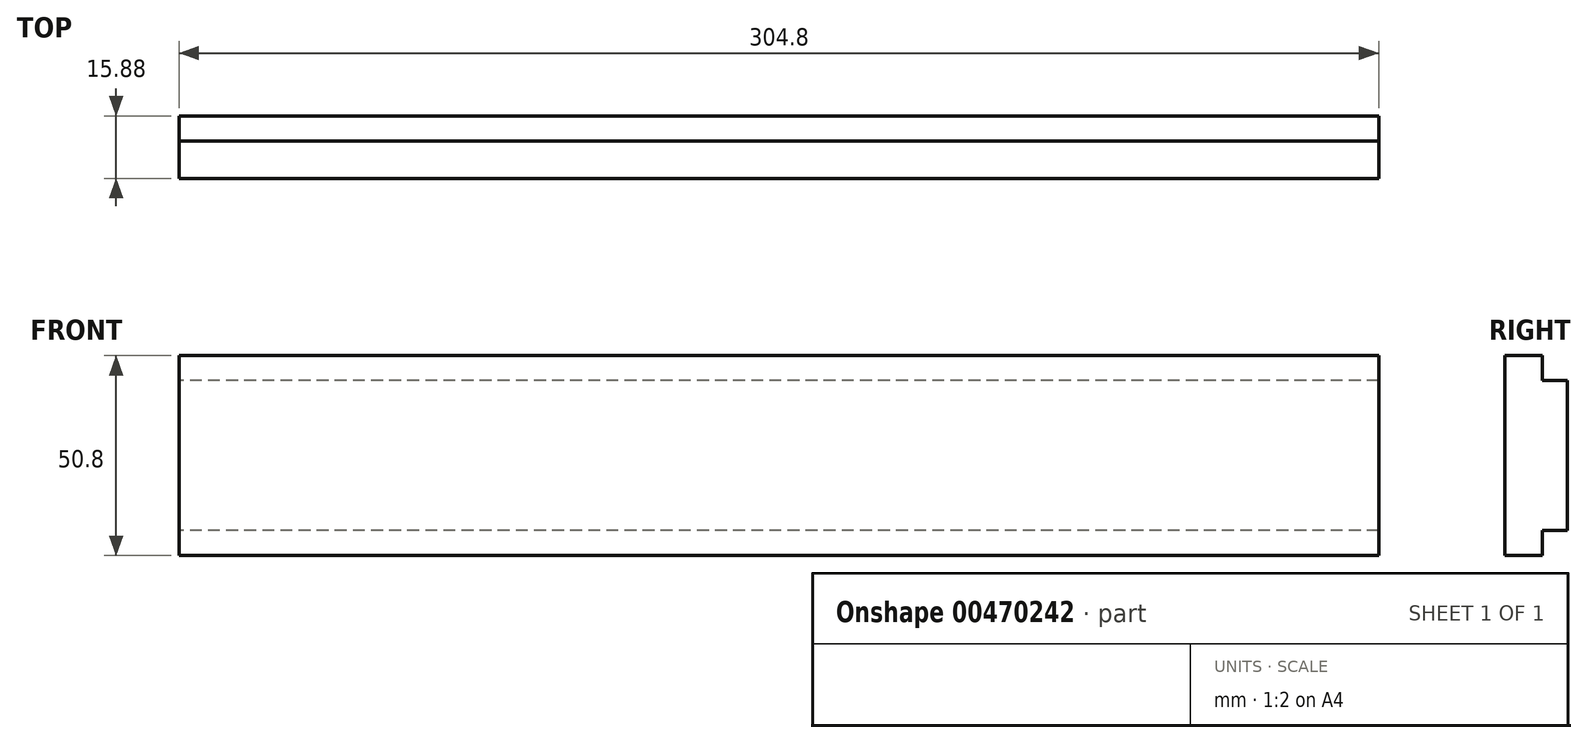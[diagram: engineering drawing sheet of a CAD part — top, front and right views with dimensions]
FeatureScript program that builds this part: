
annotation { "Feature Type Name" : "Feature", "Feature Type Description" : "" }
export const myFeature = defineFeature(function(context is Context, id is Id, definition is map)
    precondition{}
    {
        {
            var Q0;
            Q0=qCreatedBy(makeId("Right.planeOp"),FACE);
            var sketch = newSketch(context, id + "F0", { "sketchPlane" : qUnion([Q0])});
            skLineSegment(sketch, "E0.bottom", {"start": v(-20.64, 25.4) * mm, "end": v(-11.11, 25.4) * mm});
            skLineSegment(sketch, "E0.top", {"start": v(-20.64, -25.4) * mm, "end": v(-11.11, -25.4) * mm});
            skLineSegment(sketch, "E0.left", {"start": v(-20.64, 25.4) * mm, "end": v(-20.64, -25.4) * mm});
            skLineSegment(sketch, "E0.right", {"start": v(-11.11, 25.4) * mm, "end": v(-11.11, -25.4) * mm});
            skLineSegment(sketch, "E1.bottom", {"start": v(-11.11, -19.05) * mm, "end": v(-4.76, -19.05) * mm});
            skLineSegment(sketch, "E1.top", {"start": v(-11.11, 19.05) * mm, "end": v(-4.76, 19.05) * mm});
            skLineSegment(sketch, "E1.left", {"start": v(-11.11, -19.05) * mm, "end": v(-11.11, 19.05) * mm});
            skLineSegment(sketch, "E1.right", {"start": v(-4.76, -19.05) * mm, "end": v(-4.76, 19.05) * mm});
            skSolve(sketch);
        }
        {
            var Q0;
            Q0 = qSketchRegion(id + "F0", true);
            extrude(context, id + "F1", {"entities" : qUnion([Q0]), "endBound" : BoundingType.SYMMETRIC, "depth" : 304.8 * mm});
        }
    });
